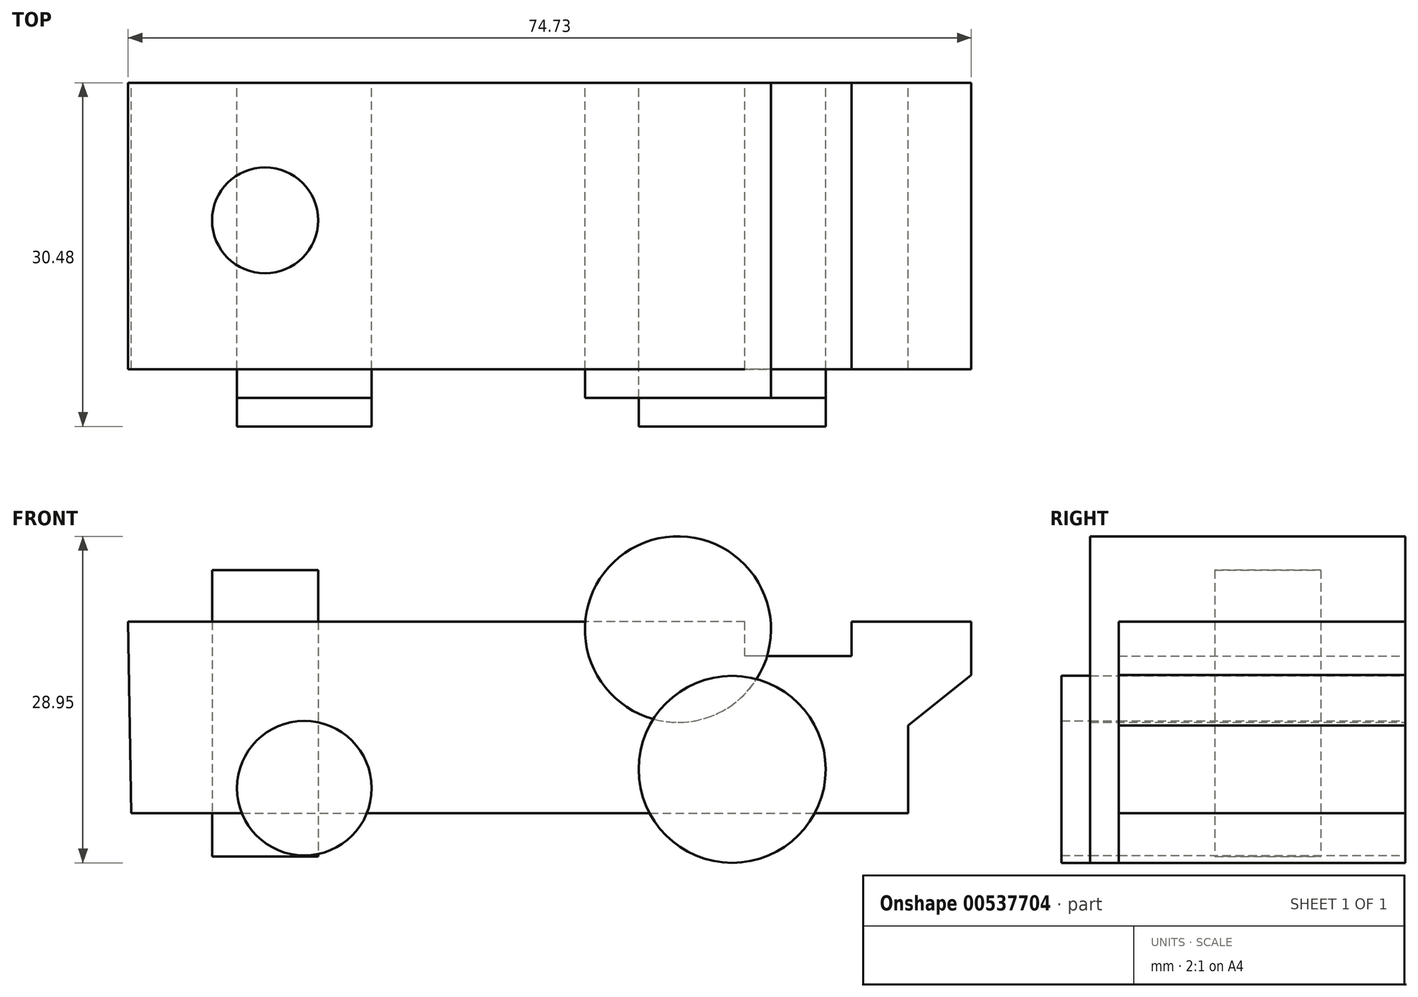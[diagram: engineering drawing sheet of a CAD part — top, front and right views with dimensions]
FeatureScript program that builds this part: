
annotation { "Feature Type Name" : "Feature", "Feature Type Description" : "" }
export const myFeature = defineFeature(function(context is Context, id is Id, definition is map)
    precondition{}
    {
        {
            var Q0;
            Q0=qCreatedBy(makeId("Front.planeOp"),FACE);
            var sketch = newSketch(context, id + "F0", { "sketchPlane" : qUnion([Q0])});
            skCircle(sketch, "E0", {"center": v(17.43, 7.73) * mm, "radius": 8.3 * mm});
            skCircle(sketch, "E1", {"center": v(-20.5, 6.06) * mm, "radius": 5.97 * mm});
            skSolve(sketch);
        }
        {
            var Q0;
            Q0=makeQuery(id+"F0.imprint","IMPRINT",FACE,{"disambiguationData":[TD([[makeQuery(id+"F0.imprint","IMPRINT",EDGE,{"derivedFrom":sQuery(id+"F0.wireOp",EDGE,"E0")}),1.0]])]});
            var Q1;
            Q1=makeQuery(id+"F0.imprint","IMPRINT",FACE,{"disambiguationData":[TD([[makeQuery(id+"F0.imprint","IMPRINT",EDGE,{"derivedFrom":sQuery(id+"F0.wireOp",EDGE,"E1")}),1.0]])]});
            extrude(context, id + "F1", {"entities" : qUnion([Q0, Q1]), "depth" : 25.4 * mm, "offsetDistance" : 25.4 * mm});
        }
        {
            var Q0;
            Q0=qCreatedBy(makeId("Front.planeOp"),FACE);
            var sketch = newSketch(context, id + "F2", { "sketchPlane" : qUnion([Q0])});
            skLineSegment(sketch, "E2", {"start": v(-35.83, 3.83) * mm, "end": v(33.05, 3.83) * mm});
            skLineSegment(sketch, "E3", {"start": v(33.05, 3.83) * mm, "end": v(33.05, 11.63) * mm});
            skLineSegment(sketch, "E4", {"start": v(33.05, 11.63) * mm, "end": v(38.62, 16.1) * mm});
            skLineSegment(sketch, "E5", {"start": v(38.62, 16.1) * mm, "end": v(38.62, 20.84) * mm});
            skLineSegment(sketch, "E6", {"start": v(38.62, 20.84) * mm, "end": v(28.03, 20.84) * mm});
            skLineSegment(sketch, "E7", {"start": v(28.03, 20.84) * mm, "end": v(28.03, 17.77) * mm});
            skLineSegment(sketch, "E8", {"start": v(28.03, 17.77) * mm, "end": v(18.55, 17.77) * mm});
            skLineSegment(sketch, "E9", {"start": v(18.55, 17.77) * mm, "end": v(18.55, 20.84) * mm});
            skLineSegment(sketch, "E10", {"start": v(18.55, 20.84) * mm, "end": v(-36.1, 20.84) * mm});
            skLineSegment(sketch, "E11", {"start": v(-36.1, 20.84) * mm, "end": v(-35.83, 3.83) * mm});
            skSolve(sketch);
        }
        {
            var Q0;
            Q0=makeQuery(id+"F2.imprint","IMPRINT",FACE,{"disambiguationData":[TD([[makeQuery(id+"F2.imprint","IMPRINT",EDGE,{"derivedFrom":sQuery(id+"F2.wireOp",EDGE,"E2")}),1.0]])]});
            extrude(context, id + "F3", {"entities" : qUnion([Q0]), "depth" : 25.4 * mm, "offsetDistance" : 25.4 * mm});
        }
        {
            var Q0;
            Q0=makeQuery(id+"F1.opExtrude","CAP_FACE",FACE,{"disambiguationData":[OSD([sQuery(id+"F0.wireOp",EDGE,"E1")])],"isStart":false});
            var Q1;
            Q1=makeQuery(id+"F1.opExtrude","CAP_FACE",FACE,{"disambiguationData":[OSD([sQuery(id+"F0.wireOp",EDGE,"E0")])],"isStart":false});
            extrude(context, id + "F4", {"entities" : qUnion([Q0, Q1]), "depth" : 2.54 * mm, "offsetDistance" : 25.4 * mm});
        }
        {
            var Q0;
            Q0=qCreatedBy(makeId("Front.planeOp"),FACE);
            var sketch = newSketch(context, id + "F5", { "sketchPlane" : qUnion([Q0])});
            skCircle(sketch, "E12", {"center": v(12.63, 20.14) * mm, "radius": 8.25 * mm});
            skSolve(sketch);
        }
        {
            var Q0;
            Q0=makeQuery(id+"F5.imprint","IMPRINT",FACE,{"disambiguationData":[TD([[makeQuery(id+"F5.imprint","IMPRINT",EDGE,{"derivedFrom":sQuery(id+"F5.wireOp",EDGE,"E12")}),1.0]])]});
            extrude(context, id + "F6", {"entities" : qUnion([Q0]), "depth" : 27.94 * mm, "offsetDistance" : 25.4 * mm});
        }
        {
            var Q0;
            Q0=makeQuery(id+"F4.opExtrude","CAP_FACE",FACE,{"disambiguationData":[OSD([sQuery(id+"F0.wireOp",EDGE,"E1")])],"isStart":false});
            var Q1;
            Q1=makeQuery(id+"F4.opExtrude","CAP_FACE",FACE,{"disambiguationData":[OSD([sQuery(id+"F0.wireOp",EDGE,"E0")])],"isStart":false});
            extrude(context, id + "F7", {"entities" : qUnion([Q0, Q1]), "depth" : 2.54 * mm, "offsetDistance" : 25.4 * mm});
        }
        {
            var Q0;
            Q0=qCreatedBy(makeId("Top.planeOp"),FACE);
            var sketch = newSketch(context, id + "F8", { "sketchPlane" : qUnion([Q0])});
            skCircle(sketch, "E13", {"center": v(-23.97, -12.2) * mm, "radius": 4.7 * mm});
            skSolve(sketch);
        }
        {
            var Q0;
            Q0=makeQuery(id+"F8.imprint","IMPRINT",FACE,{"disambiguationData":[TD([[makeQuery(id+"F8.imprint","IMPRINT",EDGE,{"derivedFrom":sQuery(id+"F8.wireOp",EDGE,"E13")}),1.0]])]});
            extrude(context, id + "F9", {"entities" : qUnion([Q0]), "depth" : 25.4 * mm, "offsetDistance" : 25.4 * mm});
        }
    });
